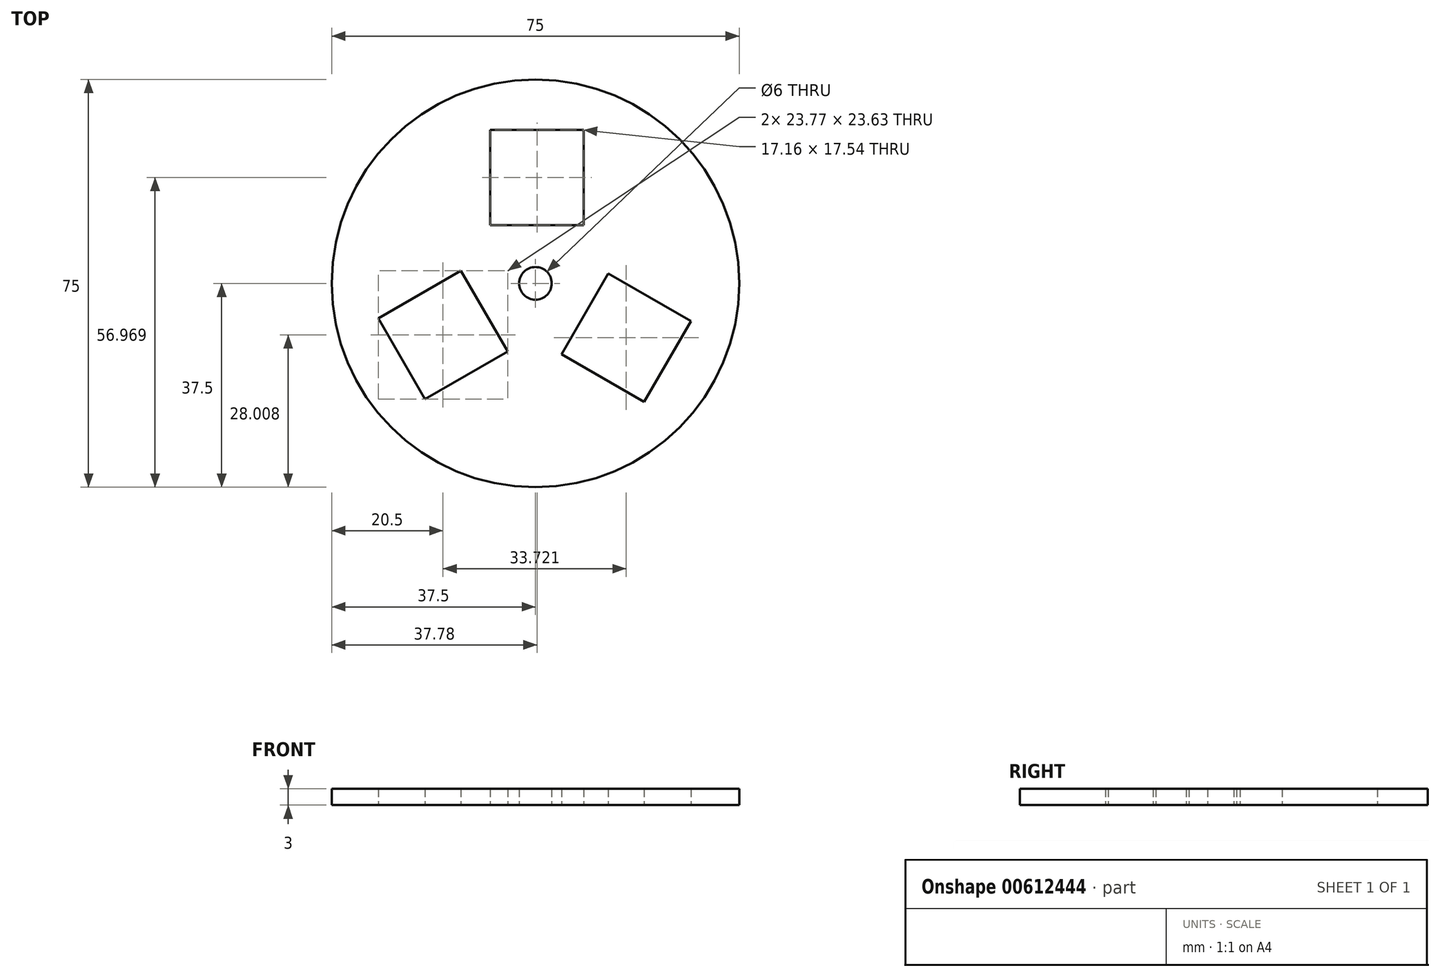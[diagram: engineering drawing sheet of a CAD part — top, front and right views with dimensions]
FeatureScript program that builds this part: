
annotation { "Feature Type Name" : "Feature", "Feature Type Description" : "" }
export const myFeature = defineFeature(function(context is Context, id is Id, definition is map)
    precondition{}
    {
        {
            var Q0;
            Q0=qCreatedBy(makeId("Top.planeOp"),FACE);
            var sketch = newSketch(context, id + "F0", { "sketchPlane" : qUnion([Q0])});
            skCircle(sketch, "E0", {"center": v(0, 0) * mm, "radius": 37.5 * mm});
            skCircle(sketch, "E1", {"center": v(0, 0) * mm, "radius": 3 * mm});
            skLineSegment(sketch, "E2.bottom", {"start": v(-8.3, 28.24) * mm, "end": v(8.86, 28.24) * mm});
            skLineSegment(sketch, "E2.top", {"start": v(-8.3, 10.7) * mm, "end": v(8.86, 10.7) * mm});
            skLineSegment(sketch, "E2.left", {"start": v(-8.3, 28.24) * mm, "end": v(-8.3, 10.7) * mm});
            skLineSegment(sketch, "E2.right", {"start": v(8.86, 28.24) * mm, "end": v(8.86, 10.7) * mm});
            skLineSegment(sketch, "E3.1.0", {"start": v(-20.3, -21.3) * mm, "end": v(-28.88, -6.45) * mm});
            skLineSegment(sketch, "E3.1.1", {"start": v(-20.3, -21.3) * mm, "end": v(-5.12, -12.54) * mm});
            skLineSegment(sketch, "E3.1.2", {"start": v(-5.12, -12.54) * mm, "end": v(-13.7, 2.32) * mm});
            skLineSegment(sketch, "E3.1.3", {"start": v(-28.88, -6.45) * mm, "end": v(-13.7, 2.32) * mm});
            skLineSegment(sketch, "E3.2.0", {"start": v(28.6, -6.93) * mm, "end": v(20.02, -21.8) * mm});
            skLineSegment(sketch, "E3.2.1", {"start": v(28.6, -6.93) * mm, "end": v(13.42, 1.84) * mm});
            skLineSegment(sketch, "E3.2.2", {"start": v(13.42, 1.84) * mm, "end": v(4.84, -13.02) * mm});
            skLineSegment(sketch, "E3.2.3", {"start": v(20.02, -21.8) * mm, "end": v(4.84, -13.02) * mm});
            skSolve(sketch);
        }
        {
            var Q0;
            Q0=makeQuery(id+"F0.imprint","IMPRINT",FACE,{"disambiguationData":[TD([[makeQuery(id+"F0.imprint","IMPRINT",EDGE,{"derivedFrom":sQuery(id+"F0.wireOp",EDGE,"E0")}),1.0]])]});
            extrude(context, id + "F1", {"entities" : qUnion([Q0]), "depth" : 3 * mm, "offsetDistance" : 25 * mm});
        }
    });
